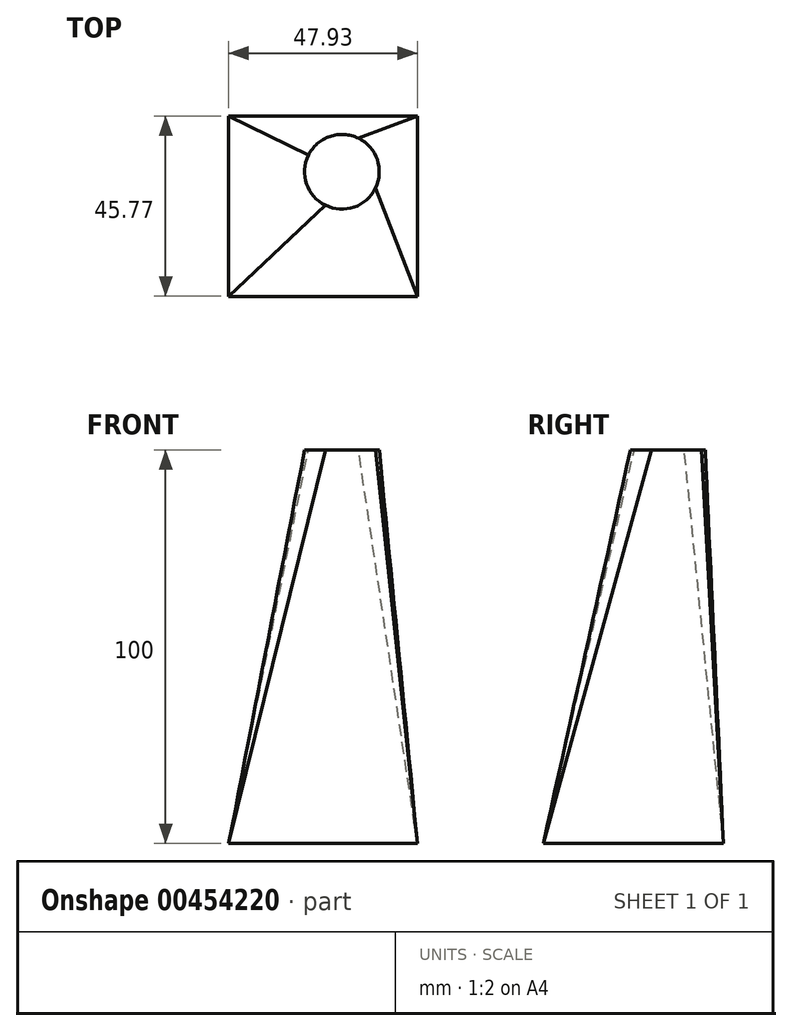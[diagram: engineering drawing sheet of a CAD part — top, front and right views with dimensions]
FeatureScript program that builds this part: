
annotation { "Feature Type Name" : "Feature", "Feature Type Description" : "" }
export const myFeature = defineFeature(function(context is Context, id is Id, definition is map)
    precondition{}
    {
        {
            var Q0;
            Q0=qCreatedBy(makeId("Top.planeOp"),FACE);
            var sketch = newSketch(context, id + "F0", { "sketchPlane" : qUnion([Q0])});
            skLineSegment(sketch, "E0.bottom", {"start": v(0, 0) * mm, "end": v(47.93, 0) * mm});
            skLineSegment(sketch, "E0.top", {"start": v(0, -45.77) * mm, "end": v(47.93, -45.77) * mm});
            skLineSegment(sketch, "E0.left", {"start": v(0, 0) * mm, "end": v(0, -45.77) * mm});
            skLineSegment(sketch, "E0.right", {"start": v(47.93, 0) * mm, "end": v(47.93, -45.77) * mm});
            skSolve(sketch);
        }
        {
            var Q0;
            Q0=qCreatedBy(makeId("Top.planeOp"),FACE);
            cPlane(context, id + "F1", {"entities" : qUnion([Q0]), "cplaneType" : CPlaneType.OFFSET, "offset" : 100 * mm, "width" : 150 * mm, "height" : 150 * mm});
        }
        {
            var Q0;
            Q0=qCreatedBy(id+"F1.planeOp",FACE);
            var sketch = newSketch(context, id + "F2", { "sketchPlane" : qUnion([Q0])});
            skCircle(sketch, "E1", {"center": v(28.76, -14.14) * mm, "radius": 9.5 * mm});
            skSolve(sketch);
        }
        {
            var Q0;
            Q0 = qSketchRegion(id + "F0", true);
            var Q1;
            Q1 = qSketchRegion(id + "F2", true);
            loft(context, id + "F3", {"sheetProfilesArray" : [{ "sheetProfileEntities" : qUnion([Q0]) }, { "sheetProfileEntities" : qUnion([Q1]) }]});
        }
    });
